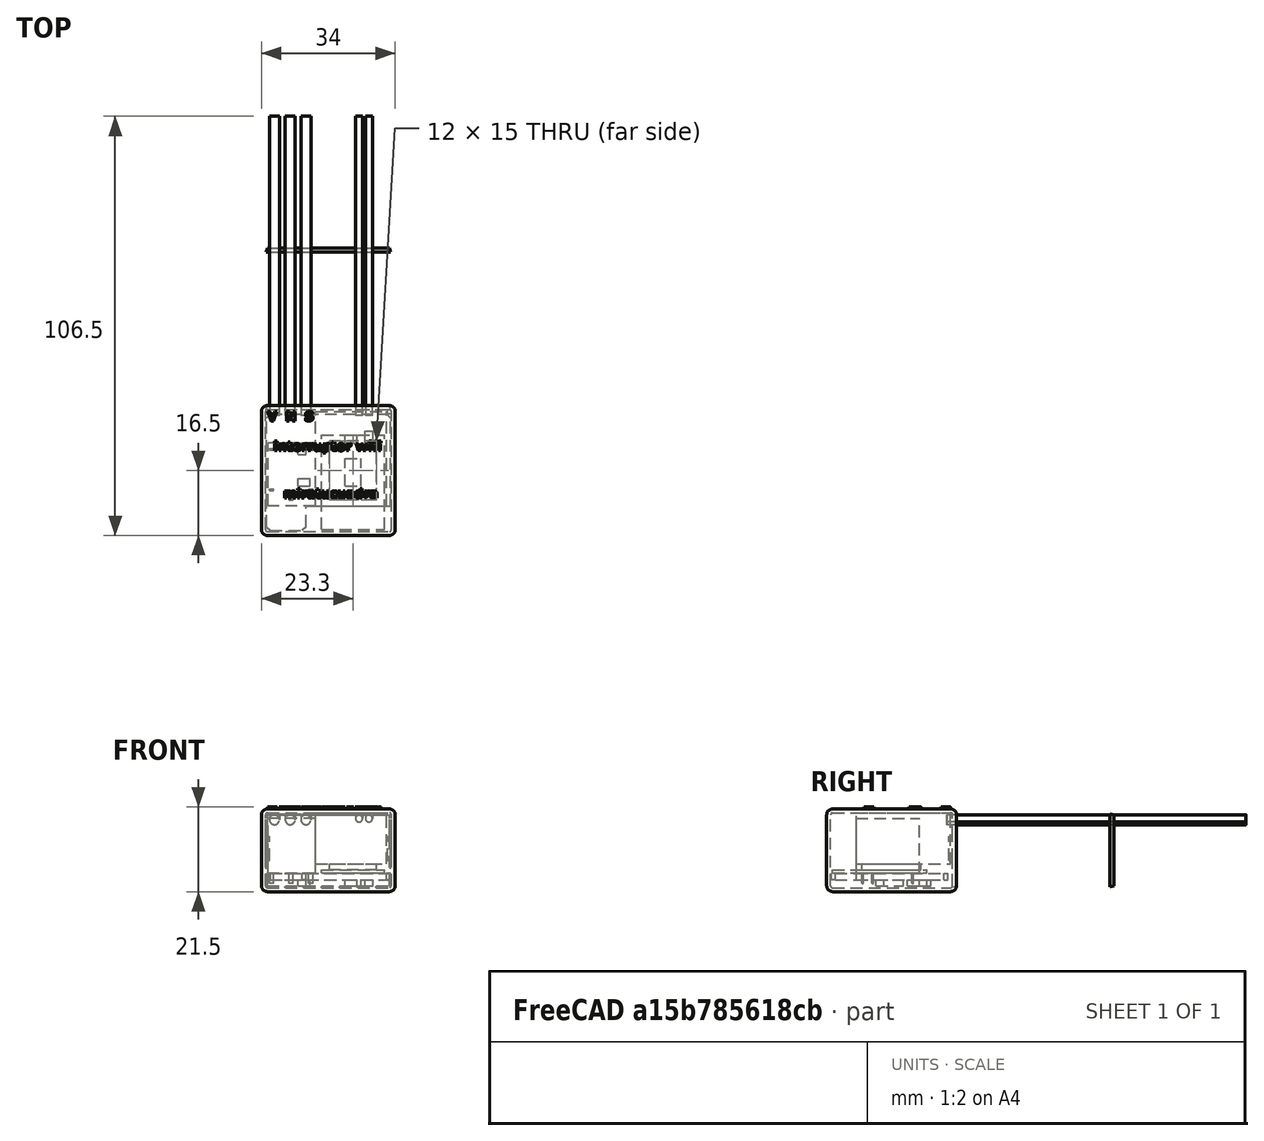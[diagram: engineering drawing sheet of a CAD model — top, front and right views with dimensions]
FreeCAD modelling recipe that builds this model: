
FCSTD DOCUMENT  (FreeCAD 0.20R29410 (Git))
Label: device01_funda_hueca
License: All rights reserved
LicenseURL: http://en.wikipedia.org/wiki/All_rights_reserved
objects: Part::Extrusion×65, Part::Feature×41, Part::Box×26, Part::Cut×11, Part::Cylinder×10, Part::MultiFuse×8, Part::Chamfer×2, Part::Fillet×2, Part::Wedge×2, App::MeasureDistance×2, Part::Fuse×1, App::DocumentObjectGroup×1
note: 168 computed .brp shape members not serialized (recipe doc carries the construction recipe); baked Part::Feature solids carry a one-line shape summary decoded from their .brp

FEATURE [Part::Box] Box  label="fuente"
  AttacherType = Attacher::AttachEngine3D
  Height = 13
  Length = 18
  Placement = pos=(12.5,0,4) rot=(0,0,1;0rad)
  Width = 24
FEATURE [Part::Box] Box002  label="placabase"
  AttacherType = Attacher::AttachEngine3D
  Height = 1.6
  Length = 31.5
  Width = 23.3
FEATURE [Part::Chamfer] Chamfer001  label="placa sin comp"
  Base = -> Box002
  Edges = 2 edges r=1: [Edge3,Edge7]
FEATURE [Part::Box] Box004  label="cuerpo"
  AttacherType = Attacher::AttachEngine3D
  Height = 14
  Length = 16
  Placement = pos=(0,0,-1) rot=(0,0,1;0rad)
  Width = 12
FEATURE [Part::Box] Box005  label="pata002"
  AttacherType = Attacher::AttachEngine3D
  Height = 4
  Length = 0.4
  Placement = pos=(1.45,5.6,-3.5) rot=(0,0,1;0rad)
  Width = 1.1
FEATURE [Part::Box] Box006  label="pata003"
  AttacherType = Attacher::AttachEngine3D
  Height = 4
  Length = 0.4
  Placement = pos=(14.15,10.6,-3.5) rot=(0,0,1;0rad)
  Width = 1.1
FEATURE [Part::Box] Box007  label="pata004"
  AttacherType = Attacher::AttachEngine3D
  Height = 4
  Length = 0.4
  Placement = pos=(3.95,10.6,-3.5) rot=(0,0,1;0rad)
  Width = 1.1
FEATURE [Part::Box] Box008  label="pata005"
  AttacherType = Attacher::AttachEngine3D
  Height = 4
  Length = 0.4
  Placement = pos=(14.15,0.6,-3.5) rot=(0,0,1;0rad)
  Width = 1.1
FEATURE [Part::Box] Box009  label="pata1"
  AttacherType = Attacher::AttachEngine3D
  Height = 4
  Length = 0.4
  Placement = pos=(3.95,0.6,-3.5) rot=(0,0,1;0rad)
  Width = 1.1
FEATURE [Part::MultiFuse] Fusion001  label="relay"
  Placement = pos=(12.4,0,2.6) rot=(0,0,1;1.5708rad)
  Shapes = -> [Box009,Box007,Box005,Box006,Box008,Box004]
FEATURE [Part::Box] Box010  label="fundaprisma"
  AttacherType = Attacher::AttachEngine3D
  Height = 21
  Length = 34
  Placement = pos=(-1.3,-7.5,-3) rot=(0,0,1;0rad)
  Width = 33
FEATURE [Part::Box] Box012  label="base8266"
  AttacherType = Attacher::AttachEngine3D
  Height = 0.8
  Length = 16
  Placement = pos=(14,-6,1.7) rot=(0,0,1;0rad)
  Width = 24
FEATURE [Part::Box] Box013  label="base8267"
  AttacherType = Attacher::AttachEngine3D
  Height = 2.3
  Length = 12
  Placement = pos=(16,1.5,1.7) rot=(0,0,1;0rad)
  Width = 15
FEATURE [Part::Fuse] Fusion  label="8266"
  Base = -> Box012
  Tool = -> Box013
FEATURE [Part::Cylinder] Cylinder  label="vivo"
  Angle = 360
  AttacherType = Attacher::AttachEngine3D
  FirstAngle = 0
  Height = 76
  Placement = pos=(2,23,15.25) rot=(-1,0,0;1.5708rad)
  Radius = 1.25
  SecondAngle = 0
FEATURE [Part::Cylinder] Cylinder001  label="neutro"
  Angle = 360
  AttacherType = Attacher::AttachEngine3D
  FirstAngle = 0
  Height = 76
  Placement = pos=(6,23,15.25) rot=(-1,0,0;1.5708rad)
  Radius = 1.25
  SecondAngle = 0
FEATURE [Part::Cylinder] Cylinder002  label="salida"
  Angle = 360
  AttacherType = Attacher::AttachEngine3D
  FirstAngle = 0
  Height = 76
  Placement = pos=(10,23,15.25) rot=(-1,0,0;1.5708rad)
  Radius = 1.25
  SecondAngle = 0
FEATURE [Part::Cylinder] Cylinder003  label="c1"
  Angle = 360
  AttacherType = Attacher::AttachEngine3D
  FirstAngle = 0
  Height = 76
  Placement = pos=(23.5,23,15.6) rot=(-1,0,0;1.5708rad)
  Radius = 0.9
  SecondAngle = 0
FEATURE [Part::Cylinder] Cylinder004  label="c2"
  Angle = 360
  AttacherType = Attacher::AttachEngine3D
  FirstAngle = 0
  Height = 76
  Placement = pos=(26,23,15.6) rot=(-1,0,0;1.5708rad)
  Radius = 0.9
  SecondAngle = 0
FEATURE [App::DocumentObjectGroup] Group  label="cables"
  Group = -> [Cylinder004,Cylinder003,Cylinder002,Cylinder001,Cylinder]
FEATURE [Part::Box] Box014  label="comp1"
  AttacherType = Attacher::AttachEngine3D
  Height = 1.6
  Length = 4
  Placement = pos=(20,5,-1.6) rot=(0,0,1;0rad)
  Width = 7
FEATURE [Part::Box] Box015  label="comp2"
  AttacherType = Attacher::AttachEngine3D
  Height = 1.6
  Length = 3
  Placement = pos=(20,16,-1.6) rot=(0,0,1;0rad)
  Width = 2
FEATURE [Part::Box] Box016  label="comp3"
  AttacherType = Attacher::AttachEngine3D
  Height = 1.6
  Length = 2
  Placement = pos=(25,16,-1.6) rot=(0,0,1;0rad)
  Width = 3
FEATURE [Part::Box] Box017  label="comp4"
  AttacherType = Attacher::AttachEngine3D
  Height = 1.6
  Length = 3
  Placement = pos=(8,5,-1.6) rot=(0,0,1;0rad)
  Width = 2
FEATURE [Part::Box] Box018  label="comp5"
  AttacherType = Attacher::AttachEngine3D
  Height = 1.6
  Length = 2
  Placement = pos=(8,13,-1.6) rot=(0,0,1;0rad)
  Width = 3
FEATURE [Part::Feature] path3990
  shape: bbox 2.35 x 2.308 x 2e-07 mm, 0 faces, 0 solids (baked)
FEATURE [Part::Extrusion] Extrude
  Base = -> path3990
  Dir = (0,0,-1)
  DirMode = 2
  FaceMakerClass = Part::FaceMakerBullseye
  LengthFwd = 1
  LengthRev = 0
  Solid = true
  Symmetric = false
FEATURE [Part::Feature] path3992
  shape: bbox 2.099 x 2.308 x 2e-07 mm, 0 faces, 0 solids (baked)
FEATURE [Part::Extrusion] Extrude001
  Base = -> path3992
  Dir = (0,0,-1)
  DirMode = 2
  FaceMakerClass = Part::FaceMakerBullseye
  LengthFwd = 1
  LengthRev = 0
  Solid = true
  Symmetric = false
FEATURE [Part::Feature] path3994
  shape: bbox 1.974 x 2.392 x 2e-07 mm, 0 faces, 0 solids (baked)
FEATURE [Part::Extrusion] Extrude002
  Base = -> path3994
  Dir = (0,0,-1)
  DirMode = 2
  FaceMakerClass = Part::FaceMakerBullseye
  LengthFwd = 1
  LengthRev = 0
  Solid = true
  Symmetric = false
FEATURE [Part::MultiFuse] Fusion003  label="v n s"
  Placement = pos=(6,23,18.5) rot=(0,0,1;0rad)
  Shapes = -> [Extrude002,Extrude,Extrude001]
FEATURE [Part::Feature] path3995
  shape: bbox 0.5581 x 1.741 x 2e-07 mm, 0 faces, 0 solids (baked)
FEATURE [Part::Extrusion] Extrude003
  Base = -> path3995
  Dir = (0,0,-1)
  DirMode = 2
  FaceMakerClass = Part::FaceMakerBullseye
  LengthFwd = 1
  LengthRev = 0
  Solid = true
  Symmetric = false
FEATURE [Part::Extrusion] Extrude022
  Base = -> path3995
  Dir = (0,0,-1)
  DirMode = 2
  FaceMakerClass = Part::FaceMakerBullseye
  LengthFwd = 1
  LengthRev = 0
  Solid = true
  Symmetric = false
FEATURE [Part::Feature] path3990001
  shape: bbox 0.5891 x 0.4232 x 2e-07 mm, 0 faces, 0 solids (baked)
FEATURE [Part::Extrusion] Extrude004
  Base = -> path3990001
  Dir = (0,0,-1)
  DirMode = 2
  FaceMakerClass = Part::FaceMakerBullseye
  LengthFwd = 1
  LengthRev = 0
  Solid = true
  Symmetric = false
FEATURE [Part::Extrusion] Extrude023
  Base = -> path3990001
  Dir = (0,0,-1)
  DirMode = 2
  FaceMakerClass = Part::FaceMakerBullseye
  LengthFwd = 1
  LengthRev = 0
  Solid = true
  Symmetric = false
FEATURE [Part::Feature] path3990002
  shape: bbox 1.749 x 1.789 x 2e-07 mm, 0 faces, 0 solids (baked)
FEATURE [Part::Extrusion] Extrude005
  Base = -> path3990002
  Dir = (0,0,-1)
  DirMode = 2
  FaceMakerClass = Part::FaceMakerBullseye
  LengthFwd = 1
  LengthRev = 0
  Solid = true
  Symmetric = false
FEATURE [Part::Extrusion] Extrude024
  Base = -> path3990002
  Dir = (0,0,-1)
  DirMode = 2
  FaceMakerClass = Part::FaceMakerBullseye
  LengthFwd = 1
  LengthRev = 0
  Solid = true
  Symmetric = false
FEATURE [Part::Feature] path3990003
  shape: bbox 1.31 x 2.273 x 2e-07 mm, 0 faces, 0 solids (baked)
FEATURE [Part::Extrusion] Extrude006
  Base = -> path3990003
  Dir = (0,0,-1)
  DirMode = 2
  FaceMakerClass = Part::FaceMakerBullseye
  LengthFwd = 1
  LengthRev = 0
  Solid = true
  Symmetric = false
FEATURE [Part::Extrusion] Extrude025
  Base = -> path3990003
  Dir = (0,0,-1)
  DirMode = 2
  FaceMakerClass = Part::FaceMakerBullseye
  LengthFwd = 1
  LengthRev = 0
  Solid = true
  Symmetric = false
FEATURE [Part::Feature] path3996
  shape: bbox 1.842 x 1.842 x 2e-07 mm, 0 faces, 0 solids (baked)
FEATURE [Part::Extrusion] Extrude007
  Base = -> path3996
  Dir = (0,0,-1)
  DirMode = 2
  FaceMakerClass = Part::FaceMakerBullseye
  LengthFwd = 1
  LengthRev = 0
  Solid = true
  Symmetric = false
FEATURE [Part::Feature] path3996001
  shape: bbox 0.724 x 0.3519 x 2e-07 mm, 0 faces, 0 solids (baked)
FEATURE [Part::Extrusion] Extrude008
  Base = -> path3996001
  Dir = (0,0,1)
  DirMode = 2
  FaceMakerClass = Part::FaceMakerBullseye
  LengthFwd = 1
  LengthRev = 0
  Placement = pos=(0,0,-1) rot=(0,0,1;0rad)
  Solid = true
  Symmetric = false
FEATURE [Part::Cut] Cut003
  Base = -> Extrude007
  Tool = -> Extrude008
FEATURE [Part::Feature] path3998
  shape: bbox 1.262 x 1.747 x 2e-07 mm, 0 faces, 0 solids (baked)
FEATURE [Part::Extrusion] Extrude009
  Base = -> path3998
  Dir = (0,0,-1)
  DirMode = 2
  FaceMakerClass = Part::FaceMakerBullseye
  LengthFwd = 1
  LengthRev = 0
  Solid = true
  Symmetric = false
FEATURE [Part::Extrusion] Extrude027
  Base = -> path3998
  Dir = (0,0,-1)
  DirMode = 2
  FaceMakerClass = Part::FaceMakerBullseye
  LengthFwd = 1
  LengthRev = 0
  Solid = true
  Symmetric = false
FEATURE [Part::Feature] path4000
  shape: bbox 1.262 x 1.747 x 2e-07 mm, 0 faces, 0 solids (baked)
FEATURE [Part::Extrusion] Extrude010
  Base = -> path4000
  Dir = (0,0,-1)
  DirMode = 2
  FaceMakerClass = Part::FaceMakerBullseye
  LengthFwd = 1
  LengthRev = 0
  Solid = true
  Symmetric = false
FEATURE [Part::Extrusion] Extrude028
  Base = -> path4000
  Dir = (0,0,-1)
  DirMode = 2
  FaceMakerClass = Part::FaceMakerBullseye
  LengthFwd = 1
  LengthRev = 0
  Solid = true
  Symmetric = false
FEATURE [Part::Feature] path4002
  shape: bbox 1.749 x 1.789 x 2e-07 mm, 0 faces, 0 solids (baked)
FEATURE [Part::Extrusion] Extrude011
  Base = -> path4002
  Dir = (0,0,-1)
  DirMode = 2
  FaceMakerClass = Part::FaceMakerBullseye
  LengthFwd = 1
  LengthRev = 0
  Solid = true
  Symmetric = false
FEATURE [Part::Extrusion] Extrude029
  Base = -> path4002
  Dir = (0,0,-1)
  DirMode = 2
  FaceMakerClass = Part::FaceMakerBullseye
  LengthFwd = 1
  LengthRev = 0
  Solid = true
  Symmetric = false
FEATURE [Part::Feature] path4004
  shape: bbox 1.817 x 2.428 x 2e-07 mm, 0 faces, 0 solids (baked)
FEATURE [Part::Extrusion] Extrude030
  Base = -> path4004
  Dir = (0,0,-1)
  DirMode = 2
  FaceMakerClass = Part::FaceMakerBullseye
  LengthFwd = 1
  LengthRev = 0
  Solid = true
  Symmetric = false
FEATURE [Part::Feature] path4004001
  shape: bbox 0.6837 x 1.003 x 2e-07 mm, 0 faces, 0 solids (baked)
FEATURE [Part::Extrusion] Extrude031
  Base = -> path4004001
  Dir = (0,0,1)
  DirMode = 2
  FaceMakerClass = Part::FaceMakerBullseye
  LengthFwd = 1
  LengthRev = 0
  Placement = pos=(0,0,-1) rot=(0,0,1;0rad)
  Solid = true
  Symmetric = false
FEATURE [Part::Cut] Cut004
  Base = -> Extrude030
  Tool = -> Extrude031
FEATURE [Part::Feature] path4006
  shape: bbox 1.31 x 2.273 x 2e-07 mm, 0 faces, 0 solids (baked)
FEATURE [Part::Extrusion] Extrude012
  Base = -> path4006
  Dir = (0,0,-1)
  DirMode = 2
  FaceMakerClass = Part::FaceMakerBullseye
  LengthFwd = 1
  LengthRev = 0
  Solid = true
  Symmetric = false
FEATURE [Part::Extrusion] Extrude032
  Base = -> path4006
  Dir = (0,0,-1)
  DirMode = 2
  FaceMakerClass = Part::FaceMakerBullseye
  LengthFwd = 1
  LengthRev = 0
  Solid = true
  Symmetric = false
FEATURE [Part::Feature] path4008
  shape: bbox 1.907 x 1.849 x 2e-07 mm, 0 faces, 0 solids (baked)
FEATURE [Part::Extrusion] Extrude013
  Base = -> path4008
  Dir = (0,0,-1)
  DirMode = 2
  FaceMakerClass = Part::FaceMakerBullseye
  LengthFwd = 1
  LengthRev = 0
  Solid = true
  Symmetric = false
FEATURE [Part::Feature] path4008001
  shape: bbox 0.7503 x 1.071 x 2e-07 mm, 0 faces, 0 solids (baked)
FEATURE [Part::Extrusion] Extrude014
  Base = -> path4008001
  Dir = (0,0,1)
  DirMode = 2
  FaceMakerClass = Part::FaceMakerBullseye
  LengthFwd = 1
  LengthRev = 0
  Placement = pos=(0,0,-1) rot=(0,0,1;0rad)
  Solid = true
  Symmetric = false
FEATURE [Part::Cut] Cut005
  Base = -> Extrude013
  Tool = -> Extrude014
FEATURE [Part::Feature] path4010
  shape: bbox 1.262 x 1.747 x 2e-07 mm, 0 faces, 0 solids (baked)
FEATURE [Part::Extrusion] Extrude015
  Base = -> path4010
  Dir = (0,0,-1)
  DirMode = 2
  FaceMakerClass = Part::FaceMakerBullseye
  LengthFwd = 1
  LengthRev = 0
  Solid = true
  Symmetric = false
FEATURE [Part::Extrusion] Extrude035
  Base = -> path4010
  Dir = (0,0,-1)
  DirMode = 2
  FaceMakerClass = Part::FaceMakerBullseye
  LengthFwd = 1
  LengthRev = 0
  Solid = true
  Symmetric = false
FEATURE [Part::Feature] path4012
  shape: bbox 2.97 x 1.741 x 2e-07 mm, 0 faces, 0 solids (baked)
FEATURE [Part::Extrusion] Extrude016
  Base = -> path4012
  Dir = (0,0,-1)
  DirMode = 2
  FaceMakerClass = Part::FaceMakerBullseye
  LengthFwd = 1
  LengthRev = 0
  Solid = true
  Symmetric = false
FEATURE [Part::Extrusion] Extrude036
  Base = -> path4012
  Dir = (0,0,-1)
  DirMode = 2
  FaceMakerClass = Part::FaceMakerBullseye
  LengthFwd = 1
  LengthRev = 0
  Solid = true
  Symmetric = false
FEATURE [Part::Feature] path4014
  shape: bbox 0.5581 x 1.741 x 2e-07 mm, 0 faces, 0 solids (baked)
FEATURE [Part::Extrusion] Extrude017
  Base = -> path4014
  Dir = (0,0,-1)
  DirMode = 2
  FaceMakerClass = Part::FaceMakerBullseye
  LengthFwd = 1
  LengthRev = 0
  Solid = true
  Symmetric = false
FEATURE [Part::Extrusion] Extrude037
  Base = -> path4014
  Dir = (0,0,-1)
  DirMode = 2
  FaceMakerClass = Part::FaceMakerBullseye
  LengthFwd = 1
  LengthRev = 0
  Solid = true
  Symmetric = false
FEATURE [Part::Feature] path4014001
  shape: bbox 0.5891 x 0.4232 x 2e-07 mm, 0 faces, 0 solids (baked)
FEATURE [Part::Extrusion] Extrude018
  Base = -> path4014001
  Dir = (0,0,-1)
  DirMode = 2
  FaceMakerClass = Part::FaceMakerBullseye
  LengthFwd = 1
  LengthRev = 0
  Solid = true
  Symmetric = false
FEATURE [Part::Extrusion] Extrude038
  Base = -> path4014001
  Dir = (0,0,-1)
  DirMode = 2
  FaceMakerClass = Part::FaceMakerBullseye
  LengthFwd = 1
  LengthRev = 0
  Solid = true
  Symmetric = false
FEATURE [Part::Feature] path4016
  shape: bbox 1.326 x 2.428 x 2e-07 mm, 0 faces, 0 solids (baked)
FEATURE [Part::Extrusion] Extrude019
  Base = -> path4016
  Dir = (0,0,-1)
  DirMode = 2
  FaceMakerClass = Part::FaceMakerBullseye
  LengthFwd = 1
  LengthRev = 0
  Solid = true
  Symmetric = false
FEATURE [Part::Extrusion] Extrude039
  Base = -> path4016
  Dir = (0,0,-1)
  DirMode = 2
  FaceMakerClass = Part::FaceMakerBullseye
  LengthFwd = 1
  LengthRev = 0
  Solid = true
  Symmetric = false
FEATURE [Part::Feature] path4018
  shape: bbox 0.5581 x 1.741 x 2e-07 mm, 0 faces, 0 solids (baked)
FEATURE [Part::Extrusion] Extrude020
  Base = -> path4018
  Dir = (0,0,-1)
  DirMode = 2
  FaceMakerClass = Part::FaceMakerBullseye
  LengthFwd = 1
  LengthRev = 0
  Solid = true
  Symmetric = false
FEATURE [Part::Extrusion] Extrude040
  Base = -> path4018
  Dir = (0,0,-1)
  DirMode = 2
  FaceMakerClass = Part::FaceMakerBullseye
  LengthFwd = 1
  LengthRev = 0
  Solid = true
  Symmetric = false
FEATURE [Part::Feature] path4018001
  shape: bbox 0.5891 x 0.4232 x 2e-07 mm, 0 faces, 0 solids (baked)
FEATURE [Part::Extrusion] Extrude021
  Base = -> path4018001
  Dir = (0,0,-1)
  DirMode = 2
  FaceMakerClass = Part::FaceMakerBullseye
  LengthFwd = 1
  LengthRev = 0
  Solid = true
  Symmetric = false
FEATURE [Part::Extrusion] Extrude041
  Base = -> path4018001
  Dir = (0,0,-1)
  DirMode = 2
  FaceMakerClass = Part::FaceMakerBullseye
  LengthFwd = 1
  LengthRev = 0
  Solid = true
  Symmetric = false
FEATURE [Part::MultiFuse] Fusion004  label="interruptores"
  Placement = pos=(9,15,18.5) rot=(0,0,1;0rad)
  Shapes = -> [Extrude003,Extrude004,Extrude005,Extrude006,Extrude009,Extrude010,Extrude011,Extrude012,Extrude015,Extrude016,Extrude017,Extrude018,Extrude019,Extrude020,Extrude021,Extrude022,Extrude023,Extrude024,Extrude025,Extrude027,Extrude028,Extrude029,Extrude032,Extrude035,Extrude036,Extrude037,Extrude038,Extrude039,Extrude040,Extrude041,Cut003,Cut004,Cut005]
FEATURE [Part::Feature] path3717
  shape: bbox 2.846 x 1.789 x 2e-07 mm, 0 faces, 0 solids (baked)
FEATURE [Part::Extrusion] Extrude042
  Base = -> path3717
  Dir = (0,0,-1)
  DirMode = 2
  FaceMakerClass = Part::FaceMakerBullseye
  LengthFwd = 1
  LengthRev = 0
  Solid = true
  Symmetric = false
FEATURE [Part::Extrusion] Extrude059
  Base = -> path3717
  Dir = (0,0,-1)
  DirMode = 2
  FaceMakerClass = Part::FaceMakerBullseye
  LengthFwd = 1
  LengthRev = 0
  Solid = true
  Symmetric = false
FEATURE [Part::Feature] path3719
  shape: bbox 0.5581 x 1.741 x 2e-07 mm, 0 faces, 0 solids (baked)
FEATURE [Part::Extrusion] Extrude043
  Base = -> path3719
  Dir = (0,0,-1)
  DirMode = 2
  FaceMakerClass = Part::FaceMakerBullseye
  LengthFwd = 1
  LengthRev = 0
  Solid = true
  Symmetric = false
FEATURE [Part::Extrusion] Extrude060
  Base = -> path3719
  Dir = (0,0,-1)
  DirMode = 2
  FaceMakerClass = Part::FaceMakerBullseye
  LengthFwd = 1
  LengthRev = 0
  Solid = true
  Symmetric = false
FEATURE [Part::Feature] path3719001
  shape: bbox 0.5891 x 0.4232 x 2e-07 mm, 0 faces, 0 solids (baked)
FEATURE [Part::Extrusion] Extrude044
  Base = -> path3719001
  Dir = (0,0,-1)
  DirMode = 2
  FaceMakerClass = Part::FaceMakerBullseye
  LengthFwd = 1
  LengthRev = 0
  Solid = true
  Symmetric = false
FEATURE [Part::Extrusion] Extrude061
  Base = -> path3719001
  Dir = (0,0,-1)
  DirMode = 2
  FaceMakerClass = Part::FaceMakerBullseye
  LengthFwd = 1
  LengthRev = 0
  Solid = true
  Symmetric = false
FEATURE [Part::Feature] path3721
  shape: bbox 1.262 x 1.747 x 2e-07 mm, 0 faces, 0 solids (baked)
FEATURE [Part::Extrusion] Extrude045
  Base = -> path3721
  Dir = (0,0,-1)
  DirMode = 2
  FaceMakerClass = Part::FaceMakerBullseye
  LengthFwd = 1
  LengthRev = 0
  Solid = true
  Symmetric = false
FEATURE [Part::Extrusion] Extrude062
  Base = -> path3721
  Dir = (0,0,-1)
  DirMode = 2
  FaceMakerClass = Part::FaceMakerBullseye
  LengthFwd = 1
  LengthRev = 0
  Solid = true
  Symmetric = false
FEATURE [Part::Feature] path3723
  shape: bbox 0.617 x 0.4868 x 2e-07 mm, 0 faces, 0 solids (baked)
FEATURE [Part::Extrusion] Extrude046
  Base = -> path3723
  Dir = (0,0,1)
  DirMode = 2
  FaceMakerClass = Part::FaceMakerBullseye
  LengthFwd = 1
  LengthRev = 0
  Placement = pos=(0,0,-1) rot=(0,0,1;0rad)
  Solid = true
  Symmetric = false
FEATURE [Part::Feature] path3723001
  shape: bbox 1.738 x 1.837 x 2e-07 mm, 0 faces, 0 solids (baked)
FEATURE [Part::Extrusion] Extrude047
  Base = -> path3723001
  Dir = (0,0,-1)
  DirMode = 2
  FaceMakerClass = Part::FaceMakerBullseye
  LengthFwd = 1
  LengthRev = 0
  Solid = true
  Symmetric = false
FEATURE [Part::Cut] Cut007
  Base = -> Extrude047
  Tool = -> Extrude046
FEATURE [Part::Feature] path3725
  shape: bbox 1.31 x 2.273 x 2e-07 mm, 0 faces, 0 solids (baked)
FEATURE [Part::Extrusion] Extrude048
  Base = -> path3725
  Dir = (0,0,-1)
  DirMode = 2
  FaceMakerClass = Part::FaceMakerBullseye
  LengthFwd = 1
  LengthRev = 0
  Solid = true
  Symmetric = false
FEATURE [Part::Extrusion] Extrude063
  Base = -> path3725
  Dir = (0,0,-1)
  DirMode = 2
  FaceMakerClass = Part::FaceMakerBullseye
  LengthFwd = 1
  LengthRev = 0
  Solid = true
  Symmetric = false
FEATURE [Part::Feature] path3727
  shape: bbox 1.749 x 1.789 x 2e-07 mm, 0 faces, 0 solids (baked)
FEATURE [Part::Extrusion] Extrude049
  Base = -> path3727
  Dir = (0,0,-1)
  DirMode = 2
  FaceMakerClass = Part::FaceMakerBullseye
  LengthFwd = 1
  LengthRev = 0
  Solid = true
  Symmetric = false
FEATURE [Part::Extrusion] Extrude064
  Base = -> path3727
  Dir = (0,0,-1)
  DirMode = 2
  FaceMakerClass = Part::FaceMakerBullseye
  LengthFwd = 1
  LengthRev = 0
  Solid = true
  Symmetric = false
FEATURE [Part::Feature] path3729
  shape: bbox 1.626 x 1.836 x 2e-07 mm, 0 faces, 0 solids (baked)
FEATURE [Part::Extrusion] Extrude050
  Base = -> path3729
  Dir = (0,0,-1)
  DirMode = 2
  FaceMakerClass = Part::FaceMakerBullseye
  LengthFwd = 1
  LengthRev = 0
  Solid = true
  Symmetric = false
FEATURE [Part::Extrusion] Extrude065
  Base = -> path3729
  Dir = (0,0,-1)
  DirMode = 2
  FaceMakerClass = Part::FaceMakerBullseye
  LengthFwd = 1
  LengthRev = 0
  Solid = true
  Symmetric = false
FEATURE [Part::Feature] path3731
  shape: bbox 1.749 x 1.789 x 2e-07 mm, 0 faces, 0 solids (baked)
FEATURE [Part::Extrusion] Extrude051
  Base = -> path3731
  Dir = (0,0,-1)
  DirMode = 2
  FaceMakerClass = Part::FaceMakerBullseye
  LengthFwd = 1
  LengthRev = 0
  Solid = true
  Symmetric = false
FEATURE [Part::Extrusion] Extrude026
  Base = -> path3731
  Dir = (0,0,-1)
  DirMode = 2
  FaceMakerClass = Part::FaceMakerBullseye
  LengthFwd = 1
  LengthRev = 0
  Solid = true
  Symmetric = false
FEATURE [Part::Feature] path3733
  shape: bbox 0.617 x 0.4868 x 2e-07 mm, 0 faces, 0 solids (baked)
FEATURE [Part::Extrusion] Extrude052
  Base = -> path3733
  Dir = (0,0,1)
  DirMode = 2
  FaceMakerClass = Part::FaceMakerBullseye
  LengthFwd = 1
  LengthRev = 0
  Placement = pos=(0,0,-1) rot=(0,0,1;0rad)
  Solid = true
  Symmetric = false
FEATURE [Part::Feature] path3733001
  shape: bbox 1.738 x 1.837 x 2e-07 mm, 0 faces, 0 solids (baked)
FEATURE [Part::Extrusion] Extrude053
  Base = -> path3733001
  Dir = (0,0,-1)
  DirMode = 2
  FaceMakerClass = Part::FaceMakerBullseye
  LengthFwd = 1
  LengthRev = 0
  Solid = true
  Symmetric = false
FEATURE [Part::Cut] Cut008
  Base = -> Extrude053
  Tool = -> Extrude052
FEATURE [Part::Feature] path3735
  shape: bbox 1.817 x 2.46 x 2e-07 mm, 0 faces, 0 solids (baked)
FEATURE [Part::Extrusion] Extrude054
  Base = -> path3735
  Dir = (0,0,-1)
  DirMode = 2
  FaceMakerClass = Part::FaceMakerBullseye
  LengthFwd = 1
  LengthRev = 0
  Solid = true
  Symmetric = false
FEATURE [Part::Feature] path3735001
  shape: bbox 0.6837 x 1.005 x 2e-07 mm, 0 faces, 0 solids (baked)
FEATURE [Part::Extrusion] Extrude055
  Base = -> path3735001
  Dir = (0,0,1)
  DirMode = 2
  FaceMakerClass = Part::FaceMakerBullseye
  LengthFwd = 1
  LengthRev = 0
  Placement = pos=(0,0,-1) rot=(0,0,1;0rad)
  Solid = true
  Symmetric = false
FEATURE [Part::Cut] Cut009
  Base = -> Extrude054
  Tool = -> Extrude055
FEATURE [Part::Feature] path3737
  shape: bbox 1.262 x 1.747 x 2e-07 mm, 0 faces, 0 solids (baked)
FEATURE [Part::Extrusion] Extrude056
  Base = -> path3737
  Dir = (0,0,-1)
  DirMode = 2
  FaceMakerClass = Part::FaceMakerBullseye
  LengthFwd = 1
  LengthRev = 0
  Solid = true
  Symmetric = false
FEATURE [Part::Extrusion] Extrude066
  Base = -> path3737
  Dir = (0,0,-1)
  DirMode = 2
  FaceMakerClass = Part::FaceMakerBullseye
  LengthFwd = 1
  LengthRev = 0
  Solid = true
  Symmetric = false
FEATURE [Part::Feature] path3739
  shape: bbox 0.617 x 0.4868 x 2e-07 mm, 0 faces, 0 solids (baked)
FEATURE [Part::Extrusion] Extrude057
  Base = -> path3739
  Dir = (0,0,1)
  DirMode = 2
  FaceMakerClass = Part::FaceMakerBullseye
  LengthFwd = 1
  LengthRev = 0
  Placement = pos=(0,0,-1) rot=(0,0,1;0rad)
  Solid = true
  Symmetric = false
FEATURE [Part::Feature] path3739001
  shape: bbox 1.738 x 1.837 x 2e-07 mm, 0 faces, 0 solids (baked)
FEATURE [Part::Extrusion] Extrude058
  Base = -> path3739001
  Dir = (0,0,-1)
  DirMode = 2
  FaceMakerClass = Part::FaceMakerBullseye
  LengthFwd = 1
  LengthRev = 0
  Solid = true
  Symmetric = false
FEATURE [Part::Cut] Cut010
  Base = -> Extrude058
  Tool = -> Extrude057
FEATURE [Part::MultiFuse] Fusion005  label="miratucuadra"
  Placement = pos=(15,3,18.5) rot=(0,0,1;0rad)
  Shapes = -> [Extrude042,Extrude043,Extrude044,Extrude045,Extrude048,Extrude049,Extrude050,Extrude051,Extrude056,Extrude059,Extrude060,Extrude061,Extrude062,Extrude063,Extrude064,Extrude065,Extrude026,Extrude066,Cut007,Cut008,Cut009,Cut010]
FEATURE [Part::Box] Box019  label="prisma int"
  AttacherType = Attacher::AttachEngine3D
  Height = 19
  Length = 32
  Placement = pos=(-0.3,-6.5,-2) rot=(0,0,1;0rad)
  Width = 31
FEATURE [Part::Box] Box003  label="placa2"
  AttacherType = Attacher::AttachEngine3D
  Height = 1.6
  Length = 10
  Placement = pos=(0,-6.3,0) rot=(0,0,1;0rad)
  Width = 6.3
FEATURE [Part::Chamfer] Chamfer
  Base = -> Box003
  Edges = 2 edges r=1: [Edge1,Edge5]
FEATURE [Part::MultiFuse] Fusion006  label="plaqueta"
  Shapes = -> [Chamfer,Chamfer001,Box014,Box015,Box016,Box017,Box018]
FEATURE [Part::Fillet] Fillet  label="externo"
  Base = -> Box010
  Edges = 12 edges r=1.5: [Edge1,Edge2,Edge3,Edge4,Edge5,Edge6,Edge7,Edge8,Edge9,Edge10,Edge11,Edge12]
FEATURE [Part::Fillet] Fillet001  label="interno"
  Base = -> Box019
  Edges = 12 edges r=0.5: [Edge1,Edge2,Edge3,Edge4,Edge5,Edge6,Edge7,Edge8,Edge9,Edge10,Edge11,Edge12]
FEATURE [Part::Cut] Cut
  Base = -> Fillet
  Tool = -> Fillet001
FEATURE [Part::Box] Box020  label="Cubo"
  AttacherType = Attacher::AttachEngine3D
  Height = 18
  Length = 31
  Placement = pos=(0.2,23,-1.5) rot=(0,0,1;0rad)
  Width = 3
FEATURE [Part::Cut] Cut011
  Base = -> Cut
  Tool = -> Box020
FEATURE [Part::Box] Box022  label="Cubo002"
  AttacherType = Attacher::AttachEngine3D
  Height = 4
  Length = 2.5
  Placement = pos=(0.75,64,15.25) rot=(0,0,1;0rad)
  Width = 3
FEATURE [Part::Box] Box023  label="Cubo003"
  AttacherType = Attacher::AttachEngine3D
  Height = 4
  Length = 2.5
  Placement = pos=(4.75,64,15.25) rot=(0,0,1;0rad)
  Width = 3
FEATURE [Part::Box] Box024  label="Cubo004"
  AttacherType = Attacher::AttachEngine3D
  Height = 4
  Length = 2.5
  Placement = pos=(8.75,64,15.25) rot=(0,0,1;0rad)
  Width = 3
FEATURE [Part::Box] Box025  label="Cubo005"
  AttacherType = Attacher::AttachEngine3D
  Height = 4
  Length = 1.8
  Placement = pos=(22.6,64,15.6) rot=(0,0,1;0rad)
  Width = 3
FEATURE [Part::Box] Box026  label="Cubo006"
  AttacherType = Attacher::AttachEngine3D
  Height = 4
  Length = 1.8
  Placement = pos=(25.1,64,15.6) rot=(0,0,1;0rad)
  Width = 3
FEATURE [Part::Cylinder] Cylinder005  label="c003"
  Angle = 360
  AttacherType = Attacher::AttachEngine3D
  FirstAngle = 0
  Height = 76
  Placement = pos=(26,23,15.6) rot=(-1,0,0;1.5708rad)
  Radius = 0.9
  SecondAngle = 0
FEATURE [Part::Cylinder] Cylinder006  label="c004"
  Angle = 360
  AttacherType = Attacher::AttachEngine3D
  FirstAngle = 0
  Height = 76
  Placement = pos=(23.5,23,15.6) rot=(-1,0,0;1.5708rad)
  Radius = 0.9
  SecondAngle = 0
FEATURE [Part::Cylinder] Cylinder007  label="salida001"
  Angle = 360
  AttacherType = Attacher::AttachEngine3D
  FirstAngle = 0
  Height = 76
  Placement = pos=(10,23,15.25) rot=(-1,0,0;1.5708rad)
  Radius = 1.25
  SecondAngle = 0
FEATURE [Part::Cylinder] Cylinder008  label="neutro001"
  Angle = 360
  AttacherType = Attacher::AttachEngine3D
  FirstAngle = 0
  Height = 76
  Placement = pos=(6,23,15.25) rot=(-1,0,0;1.5708rad)
  Radius = 1.25
  SecondAngle = 0
FEATURE [Part::Cylinder] Cylinder009  label="vivo001"
  Angle = 360
  AttacherType = Attacher::AttachEngine3D
  FirstAngle = 0
  Height = 76
  Placement = pos=(2,23,15.25) rot=(-1,0,0;1.5708rad)
  Radius = 1.25
  SecondAngle = 0
FEATURE [Part::MultiFuse] Fusion007
  Shapes = -> [Cylinder009,Box022,Box023,Box024,Box025,Box026,Cylinder005,Cylinder006,Cylinder007,Cylinder008]
FEATURE [Part::Wedge] Wedge  label="Cuña"
  AttacherType = Attacher::AttachEngine3D
  Placement = pos=(-0.1,64.5,-1.8) rot=(0,0,1;0rad)
  X2max = 31.3
  X2min = 0.3
  Xmax = 31.6
  Xmin = 0
  Ymax = 1
  Ymin = 0
  Z2max = 18.3
  Z2min = 0.3
  Zmax = 18.6
  Zmin = 0
FEATURE [Part::Wedge] Wedge001  label="Cuña001"
  AttacherType = Attacher::AttachEngine3D
  Placement = pos=(-0.1,24.5,-1.8) rot=(0,0,1;0rad)
  X2max = 31.3
  X2min = 0.3
  Xmax = 31.6
  Xmin = 0
  Ymax = 1
  Ymin = 0
  Z2max = 18.3
  Z2min = 0.3
  Zmax = 18.6
  Zmin = 0
FEATURE [Part::Cut] Cut012  label="carcasa sin texto"
  Base = -> Cut011
  Tool = -> Wedge001
FEATURE [Part::Cut] Cut013  label="tapa"
  Base = -> Wedge
  Tool = -> Fusion007
FEATURE [Part::Box] Box028  label="Cubo008"
  AttacherType = Attacher::AttachEngine3D
  Height = 6
  Length = 1
  Placement = pos=(-0.3,23.5,5) rot=(0,0,1;0rad)
  Width = 1
FEATURE [Part::Box] Box029  label="Cubo009"
  AttacherType = Attacher::AttachEngine3D
  Height = 6
  Length = 1
  Placement = pos=(30.7,23.5,5) rot=(0,0,1;0rad)
  Width = 1
FEATURE [Part::MultiFuse] Fusion008
  Shapes = -> [Box029,Box028,Cut012]
FEATURE [Part::MultiFuse] Fusion009  label="carcaza"
  Shapes = -> [Fusion008,Fusion003,Fusion004,Fusion005]
FEATURE [App::MeasureDistance] Distance  label="Distance: 31,00 mm"
  Distance = 31
  P1 = (31.2,25.5,-1.5)
  P2 = (0.2,25.5,-1.5)
FEATURE [App::MeasureDistance] Distance001  label="Distance: 31,57 mm"
  Distance = 31.5679
  P1 = (31.5,64.5,16.8)
  P2 = (-0.0676542,64.6078,16.7677)
